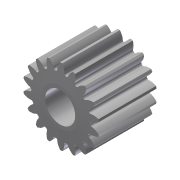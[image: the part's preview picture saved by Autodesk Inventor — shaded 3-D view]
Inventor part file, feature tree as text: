
AUTODESK INVENTOR PART (.ipt)
format: ipt  version: 2013 (Build 170138000, 138)  size: 310,784 bytes
history: native  units: in
note: dims shown in document units (in); Inventor stores cm internally (conversion verified against a paired STEP export)
features: mirror x1, other x1, imported_body x1
ambient origin geometry x8: Origin, YZ Plane, XZ Plane, XY Plane, X Axis, Y Axis, Z Axis, Center Point
feature tree (3):
  mirror  "Mirror2"
  other  "217-2724-003 Rev1_Planet_Revolving_Follower011"
  imported_body  "Base1"
